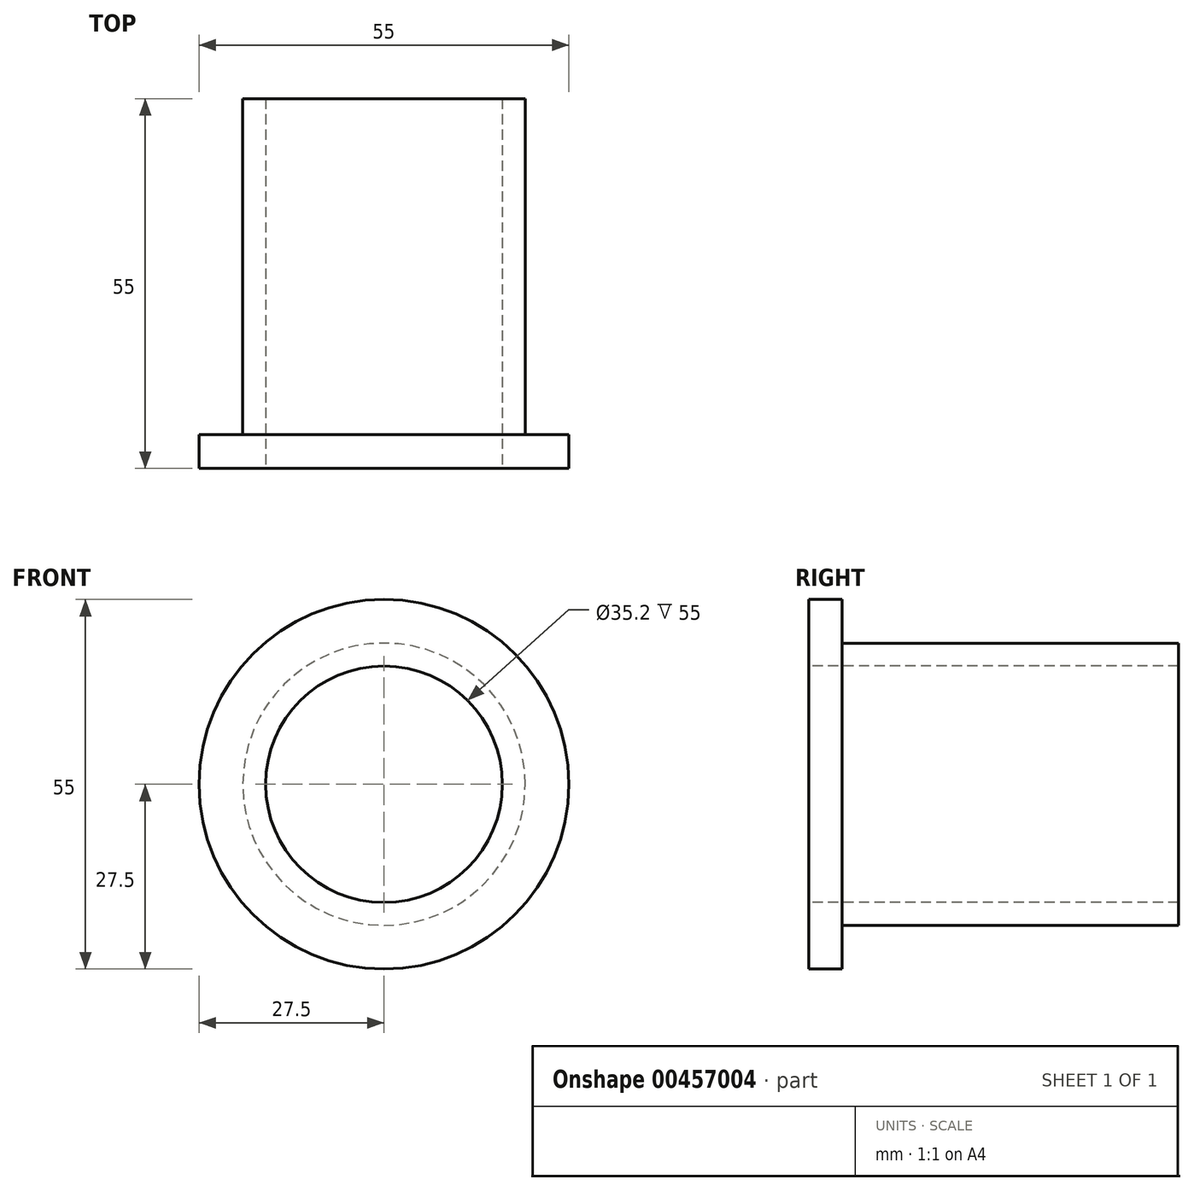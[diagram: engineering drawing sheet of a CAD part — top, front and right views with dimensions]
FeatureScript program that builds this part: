
annotation { "Feature Type Name" : "Feature", "Feature Type Description" : "" }
export const myFeature = defineFeature(function(context is Context, id is Id, definition is map)
    precondition{}
    {
        {
            var Q0;
            Q0=qCreatedBy(makeId("Front.planeOp"),FACE);
            var sketch = newSketch(context, id + "F0", { "sketchPlane" : qUnion([Q0])});
            skCircle(sketch, "E0", {"center": v(0, 0) * mm, "radius": 27.5 * mm});
            skSolve(sketch);
        }
        {
            var Q0;
            Q0=makeQuery(id+"F0.imprint","IMPRINT",FACE,{"disambiguationData":[TD([[makeQuery(id+"F0.imprint","IMPRINT",EDGE,{"derivedFrom":sQuery(id+"F0.wireOp",EDGE,"E0")}),1.0]])]});
            extrude(context, id + "F1", {"entities" : qUnion([Q0]), "oppositeDirection" : true, "depth" : 55 * mm});
        }
        {
            var Q0;
            Q0=makeQuery(id+"F1.opExtrude","CAP_FACE",FACE,{"disambiguationData":[OSD([sQuery(id+"F0.wireOp",EDGE,"E0")])],"isStart":false});
            var sketch = newSketch(context, id + "F2", { "sketchPlane" : qUnion([Q0])});
            skCircle(sketch, "E1", {"center": v(0, 0) * mm, "radius": 21 * mm});
            skSolve(sketch);
        }
        {
            var Q0;
            Q0=makeQuery(id+"F2.imprint","IMPRINT",FACE,{"disambiguationData":[TD([[makeQuery(id+"F2.imprint","IMPRINT",EDGE,{"derivedFrom":sQuery(id+"F2.wireOp",EDGE,"E1")}),-1.0]])]});
            extrude(context, id + "F3", {"entities" : qUnion([Q0]), "operationType" : NewBodyOperationType.REMOVE, "oppositeDirection" : true, "depth" : 50 * mm});
        }
        {
            var Q0;
            Q0=makeQuery(id+"F1.opExtrude","CAP_FACE",FACE,{"disambiguationData":[OSD([sQuery(id+"F0.wireOp",EDGE,"E0")])],"isStart":true});
            var sketch = newSketch(context, id + "F4", { "sketchPlane" : qUnion([Q0])});
            skCircle(sketch, "E2", {"center": v(0, 0) * mm, "radius": 8.03 * mm});
            skSolve(sketch);
        }
        {
            var Q0;
            Q0=sQuery(id+"F4.wireOp",VERTEX,"E2.center");
            var Q1;
            Q1=makeQuery(id+"F1.opExtrude","SWEPT_BODY",BODY,{"disambiguationData":[OSD([sQuery(id+"F0.wireOp",EDGE,"E0")])]});
            hole(context, id + "F5", {"style" : HoleStyle.SIMPLE, "endStyle" : HoleEndStyle.THROUGH, "holeDiameter" : 35.2 * mm, "isTappedThrough" : true, "tappedDepth" : 12 * mm, "tapClearance" : 3, "locations" : qUnion([Q0]), "scope" : qUnion([Q1])});
        }
    });
